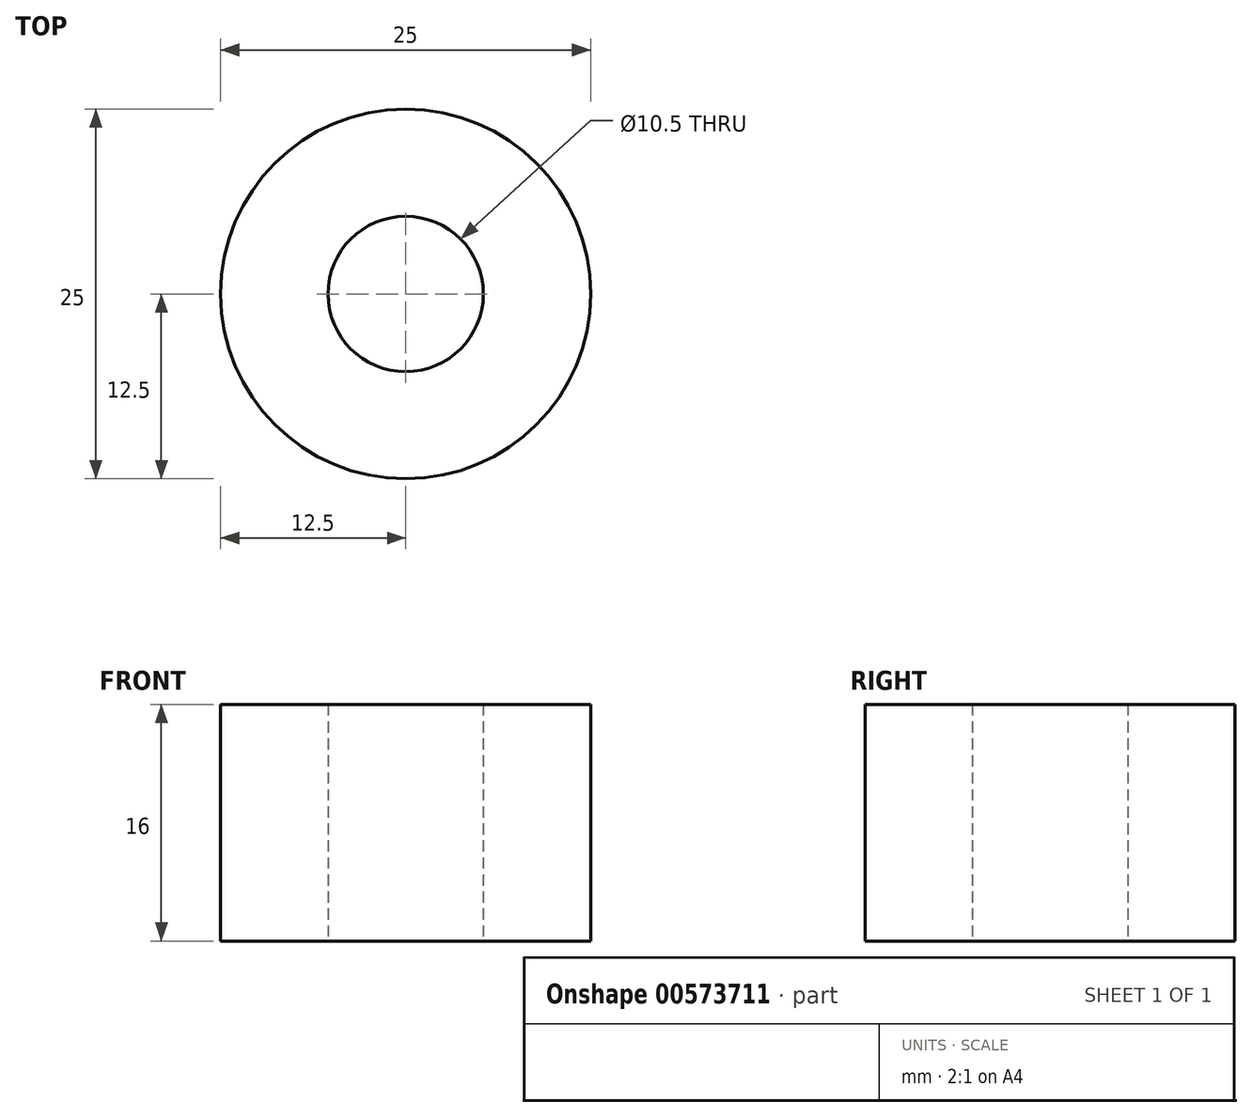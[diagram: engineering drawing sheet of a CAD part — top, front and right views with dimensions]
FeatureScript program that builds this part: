
annotation { "Feature Type Name" : "Feature", "Feature Type Description" : "" }
export const myFeature = defineFeature(function(context is Context, id is Id, definition is map)
    precondition{}
    {
        {
            var Q0;
            Q0=qCreatedBy(makeId("Top.planeOp"),FACE);
            var sketch = newSketch(context, id + "F0", { "sketchPlane" : qUnion([Q0])});
            skCircle(sketch, "E0", {"center": v(0, 0) * mm, "radius": 12.5 * mm});
            skCircle(sketch, "E1", {"center": v(0, 0) * mm, "radius": 5.25 * mm});
            skSolve(sketch);
        }
        {
            var Q0;
            Q0 = qSketchRegion(id + "F0", true);
            extrude(context, id + "F1", {"entities" : qUnion([Q0]), "depth" : 16 * mm, "offsetDistance" : 25 * mm});
        }
    });
